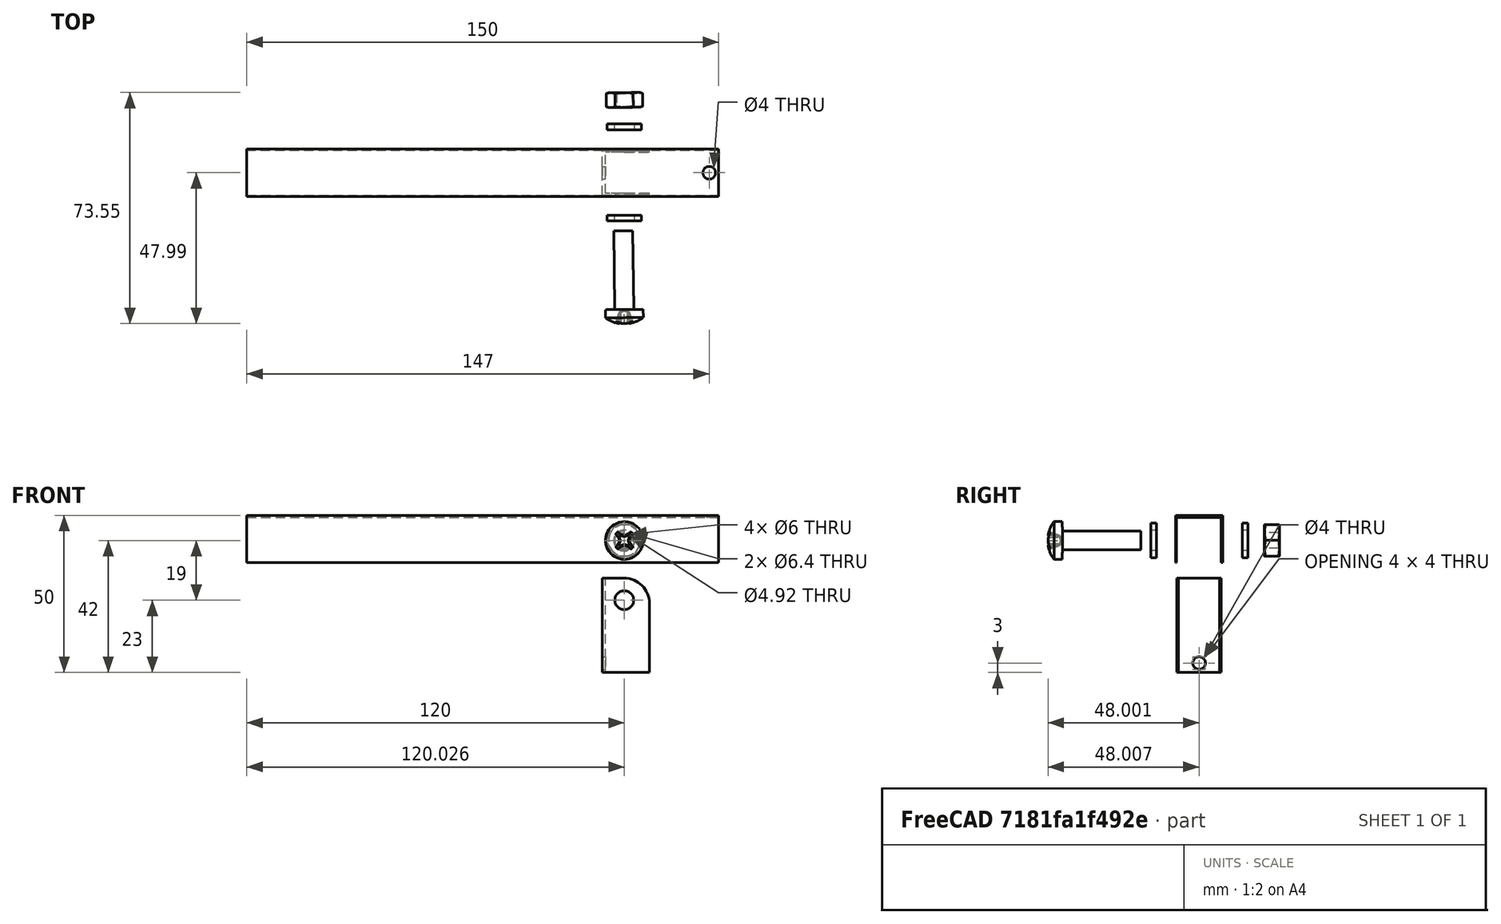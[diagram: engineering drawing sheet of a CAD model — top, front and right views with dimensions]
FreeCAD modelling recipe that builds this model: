
FCSTD DOCUMENT  (FreeCAD 0.15R4671 (Git))
Label: Cutter Lever Hinge Assy
License: All rights reserved
LicenseURL: http://en.wikipedia.org/wiki/All_rights_reserved
objects: Part::FeaturePython×6
note: 6 computed .brp shape members not serialized (recipe doc carries the construction recipe); baked Part::Feature solids carry a one-line shape summary decoded from their .brp

FEATURE [Part::FeaturePython] Washer  label="M6-Washer"  # Fasteners workbench fastener (typed FeaturePython)
  Placement = pos=(120,-8,7) rot=(1,0,0;1.5708rad)
  diameter = 7
  invert = false
  matchOuter = false
  offset = 0
  type = 2
FEATURE [Part::FeaturePython] Cutter_Lever_01  # a2plus imported part (geometry in sourceFile) (typed FeaturePython)
  Placement = pos=(0,-2,0) rot=(0,0,1;0rad)
  fixedPosition = true
  sourceFile = <path> Lever.FCStd
  timeLastImport = 1.53411e+09
  updateColors = true
FEATURE [Part::FeaturePython] Washer001  label="M6-Washer001"  # Fasteners workbench fastener (typed FeaturePython)
  Placement = pos=(120,21,7) rot=(1,0,0;1.5708rad)
  diameter = 7
  invert = false
  matchOuter = false
  offset = 0
  type = 2
FEATURE [Part::FeaturePython] Screw  label="M6x25-Screw"  # Fasteners workbench fastener (typed FeaturePython)
  Placement = pos=(120,-38,7) rot=(0.999938,0,0.01111;1.5708rad)
  diameter = 8
  invert = false
  length = 6
  matchOuter = false
  offset = 0
  thread = false
  type = 16
FEATURE [Part::FeaturePython] Nut  label="M6-Nut"  # Fasteners workbench fastener (typed FeaturePython)
  Placement = pos=(120,31,7) rot=(0.999938,0,0.01111;1.5708rad)
  diameter = 8
  invert = false
  matchOuter = false
  offset = 0
  thread = false
  type = 1
FEATURE [Part::FeaturePython] Cutter_Lever_Hinge2_01  # a2plus imported part (geometry in sourceFile) (typed FeaturePython)
  Placement = pos=(-1,0,-19) rot=(0,0,1;0rad)
  fixedPosition = false
  sourceFile = <path> Lever Hinge2.FCStd
  timeLastImport = 1.53412e+09
  updateColors = true
note: 2 file-system paths scrubbed to <path> (originals preserved in the JSON sidecar)
